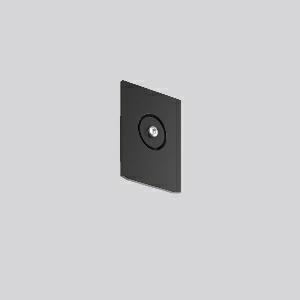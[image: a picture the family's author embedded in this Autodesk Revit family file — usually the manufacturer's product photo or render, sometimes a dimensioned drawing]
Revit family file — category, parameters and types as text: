
# Revit family: linedo_endkappe_s_f_982699_003_e9aa
name_source: partatom
category: Lighting Fixtures
units: mm (PartAtom-declared; Revit-internal decimal feet)

## family parameters
Cut with Voids When Loaded = No
Host = Face
Light Source = No
Part Type = Normal
Room Calculation Point = No
Round Connector Dimension = Use Diameter
Shared = No

## types (1)
- LINEDO_Endkappe_S_F
    Apparent Load = 0 VA
    Default Elevation = 1800 mm
    Description = End cap low profile for LINEDO socket. Plastic end cap to cover the LINEDO plug system at the end of the line. Fastening by TX20 screw. Installation accessories included.
Colour: black
Length: 16 mm
Width: 58 mm
Height: 76 mm
Weight: 21,5 g
    Height = 76 mm
    Lamp = 0 x
    Length = 17 mm
    Luminous efficacy = 0 lm/W
    Manufacturer = RZB
    ModVariant = No
    Model = 982699.003
    Mounting Place = Ceiling
    Mounting Type = Pendant, Surface mounted
    Number of Poles = 1
    OnlyDefault = Yes
    Power Factor = 1
    Product Name = LINEDO_Endkappe_S_F
    Product group = Surface mounted continuous line luminaire system
    ProductGroupID = 310
    Protection Class = Protection class
    Protection Degree = Degree of protection
    RLX_Detail_Level = 1
    RLX_Emergency_Light_Flux = 0 lm
    RLX_Emergency_Type = 0
    RLX_Emergency_Type_DB = No
    RlxData = <blob elided: 9345 chars, md5=8d0c8445>
    Standby Power = 0 W
    System Light Flux = 0 lm
    System Power = 0 W
    Type Comments = Product without accessories
    Type Image = 982699.003.jpg
    URL = http://relux.com
    VarID = ---
    Voltage = 0 V
    Weight = 0.00 kg
    Width = 58 mm

## geometry (parser evidence)
native form markers: Sweep x10
no freeform markers — native parametric forms only
